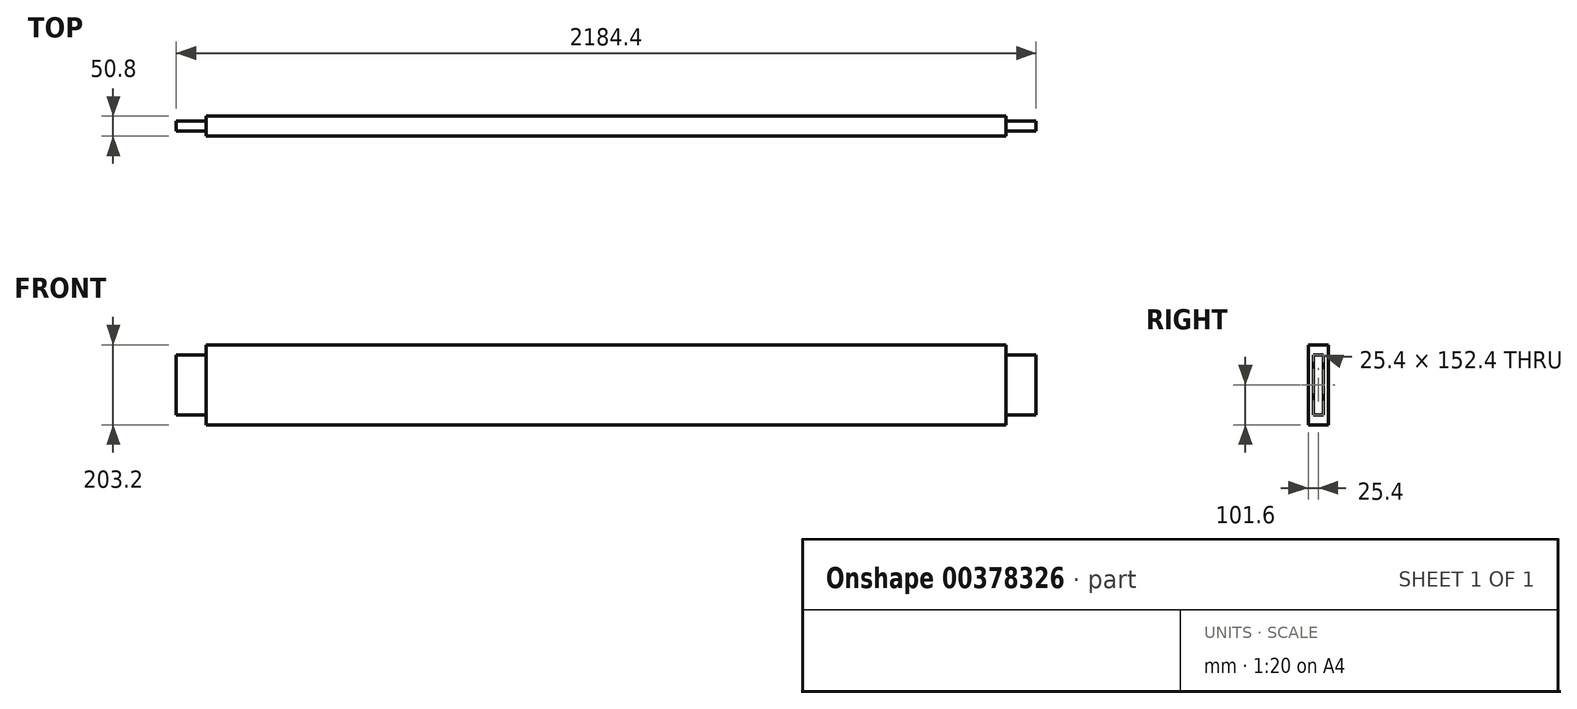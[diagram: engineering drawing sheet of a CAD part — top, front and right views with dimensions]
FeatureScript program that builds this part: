
annotation { "Feature Type Name" : "Feature", "Feature Type Description" : "" }
export const myFeature = defineFeature(function(context is Context, id is Id, definition is map)
    precondition{}
    {
        {
            var Q0;
            Q0=qCreatedBy(makeId("Front.planeOp"),FACE);
            var sketch = newSketch(context, id + "F0", { "sketchPlane" : qUnion([Q0])});
            skLineSegment(sketch, "E0.bottom", {"start": v(-1016, 101.6) * mm, "end": v(1016, 101.6) * mm});
            skLineSegment(sketch, "E0.top", {"start": v(-1016, -101.6) * mm, "end": v(1016, -101.6) * mm});
            skLineSegment(sketch, "E0.left", {"start": v(-1016, 101.6) * mm, "end": v(-1016, -101.6) * mm});
            skLineSegment(sketch, "E0.right", {"start": v(1016, 101.6) * mm, "end": v(1016, -101.6) * mm});
            skSolve(sketch);
        }
        {
            var Q0;
            Q0=makeQuery(id+"F0.imprint","IMPRINT",FACE,{"disambiguationData":[TD([[makeQuery(id+"F0.imprint","IMPRINT",EDGE,{"derivedFrom":sQuery(id+"F0.wireOp",EDGE,"E0.bottom")}),-1.0]])]});
            extrude(context, id + "F1", {"entities" : qUnion([Q0]), "depth" : 25.4 * mm, "hasSecondDirection" : true, "secondDirectionOppositeDirection" : true, "secondDirectionDepth" : 25.4 * mm});
        }
        {
            var Q0;
            Q0=makeQuery(id+"F1.opExtrude","SWEPT_FACE",FACE,{"disambiguationData":[OSD([sQuery(id+"F0.wireOp",EDGE,"E0.right")])]});
            var sketch = newSketch(context, id + "F2", { "sketchPlane" : qUnion([Q0])});
            skLineSegment(sketch, "E1.bottom", {"start": v(-12.7, 76.2) * mm, "end": v(12.7, 76.2) * mm});
            skLineSegment(sketch, "E1.top", {"start": v(-12.7, -76.2) * mm, "end": v(12.7, -76.2) * mm});
            skLineSegment(sketch, "E1.left", {"start": v(-12.7, 76.2) * mm, "end": v(-12.7, -76.2) * mm});
            skLineSegment(sketch, "E1.right", {"start": v(12.7, 76.2) * mm, "end": v(12.7, -76.2) * mm});
            skSolve(sketch);
        }
        {
            var Q0;
            Q0=makeQuery(id+"F2.imprint","IMPRINT",FACE,{"disambiguationData":[TD([[makeQuery(id+"F2.imprint","IMPRINT",EDGE,{"derivedFrom":sQuery(id+"F2.wireOp",EDGE,"E1.bottom")}),-1.0]])]});
            extrude(context, id + "F3", {"entities" : qUnion([Q0]), "operationType" : NewBodyOperationType.ADD, "depth" : 76.2 * mm});
        }
        {
            var Q0;
            Q0=makeQuery(id+"F1.opExtrude","SWEPT_FACE",FACE,{"disambiguationData":[OSD([sQuery(id+"F0.wireOp",EDGE,"E0.left")])]});
            var sketch = newSketch(context, id + "F4", { "sketchPlane" : qUnion([Q0])});
            skLineSegment(sketch, "E2.bottom", {"start": v(-12.7, 76.2) * mm, "end": v(12.7, 76.2) * mm});
            skLineSegment(sketch, "E2.top", {"start": v(-12.7, -76.2) * mm, "end": v(12.7, -76.2) * mm});
            skLineSegment(sketch, "E2.left", {"start": v(-12.7, 76.2) * mm, "end": v(-12.7, -76.2) * mm});
            skLineSegment(sketch, "E2.right", {"start": v(12.7, 76.2) * mm, "end": v(12.7, -76.2) * mm});
            skSolve(sketch);
        }
        {
            var Q0;
            Q0=makeQuery(id+"F4.imprint","IMPRINT",FACE,{"disambiguationData":[TD([[makeQuery(id+"F4.imprint","IMPRINT",EDGE,{"derivedFrom":sQuery(id+"F4.wireOp",EDGE,"E2.bottom")}),-1.0]])]});
            extrude(context, id + "F5", {"entities" : qUnion([Q0]), "operationType" : NewBodyOperationType.ADD, "depth" : 76.2 * mm});
        }
    });
